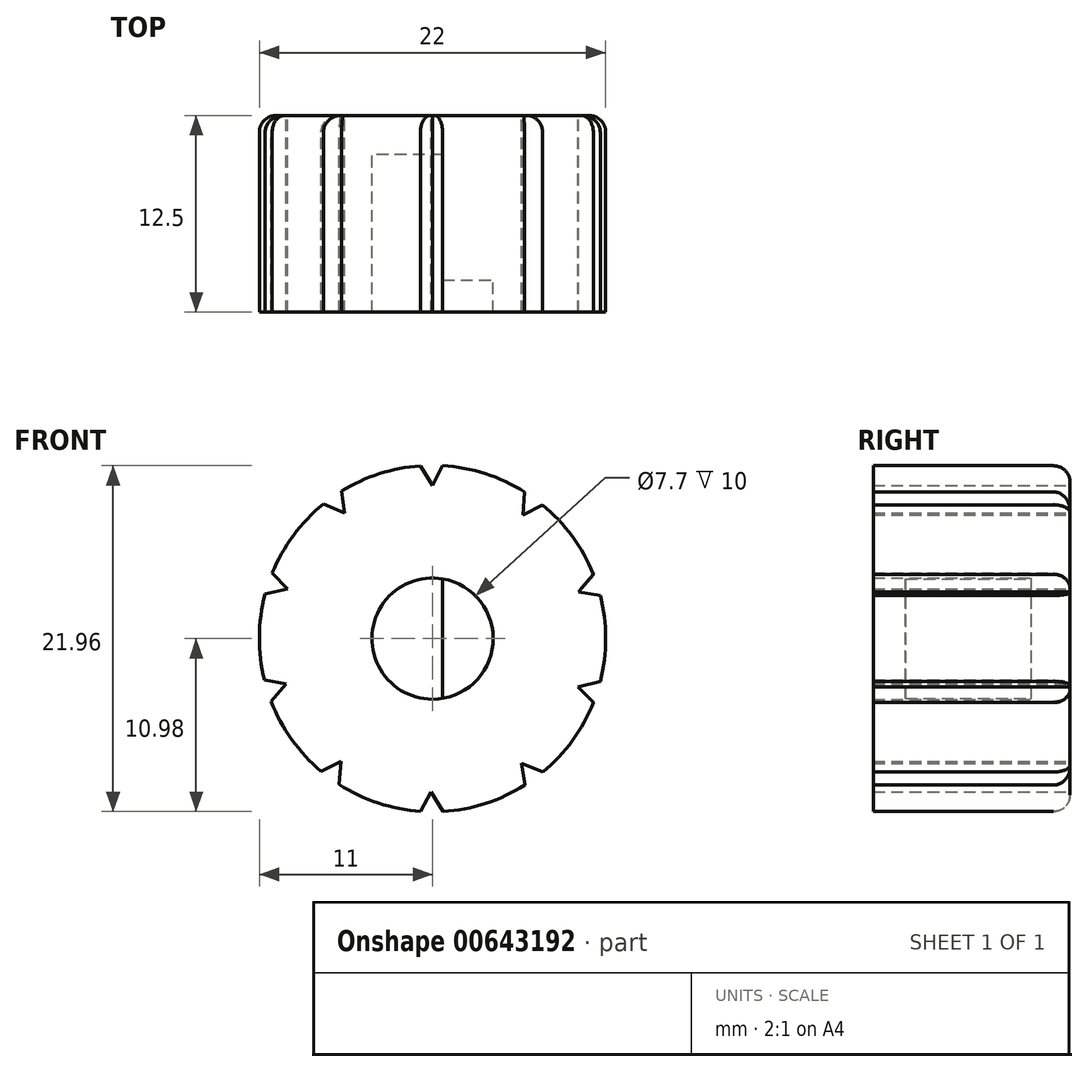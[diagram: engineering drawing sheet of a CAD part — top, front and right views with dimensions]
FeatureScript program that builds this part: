
annotation { "Feature Type Name" : "Feature", "Feature Type Description" : "" }
export const myFeature = defineFeature(function(context is Context, id is Id, definition is map)
    precondition{}
    {
        {
            var Q0;
            Q0=qCreatedBy(makeId("Front.planeOp"),FACE);
            var sketch = newSketch(context, id + "F0", { "sketchPlane" : qUnion([Q0])});
            skCircle(sketch, "E0", {"center": v(0, 0) * mm, "radius": 11 * mm});
            skCircle(sketch, "E1", {"center": v(0, 0) * mm, "radius": 3.85 * mm});
            skLineSegment(sketch, "E2", {"start": v(0.65, 3.8) * mm, "end": v(0.65, -3.8) * mm});
            skLineSegment(sketch, "E3", {"start": v(-0.77, 10.97) * mm, "end": v(0, 9.74) * mm});
            skLineSegment(sketch, "E4", {"start": v(0, 9.74) * mm, "end": v(0.64, 10.98) * mm});
            skLineSegment(sketch, "E5.1.0", {"start": v(5.74, 7.87) * mm, "end": v(6.99, 8.5) * mm});
            skLineSegment(sketch, "E5.1.1", {"start": v(5.84, 9.32) * mm, "end": v(5.74, 7.87) * mm});
            skLineSegment(sketch, "E5.2.0", {"start": v(9.27, 2.97) * mm, "end": v(10.65, 2.74) * mm});
            skLineSegment(sketch, "E5.2.1", {"start": v(10.21, 4.09) * mm, "end": v(9.27, 2.97) * mm});
            skLineSegment(sketch, "E5.3.0", {"start": v(9.24, -3.06) * mm, "end": v(10.22, -4.06) * mm});
            skLineSegment(sketch, "E5.3.1", {"start": v(10.66, -2.72) * mm, "end": v(9.24, -3.06) * mm});
            skLineSegment(sketch, "E5.4.0", {"start": v(5.66, -7.92) * mm, "end": v(5.86, -9.3) * mm});
            skLineSegment(sketch, "E5.4.1", {"start": v(7.01, -8.48) * mm, "end": v(5.66, -7.92) * mm});
            skLineSegment(sketch, "E5.5.0", {"start": v(-0.1, -9.74) * mm, "end": v(-0.75, -10.97) * mm});
            skLineSegment(sketch, "E5.5.1", {"start": v(0.67, -10.98) * mm, "end": v(-0.1, -9.74) * mm});
            skLineSegment(sketch, "E5.6.0", {"start": v(-5.81, -7.81) * mm, "end": v(-7.07, -8.43) * mm});
            skLineSegment(sketch, "E5.6.1", {"start": v(-5.93, -9.26) * mm, "end": v(-5.81, -7.81) * mm});
            skLineSegment(sketch, "E5.7.0", {"start": v(-9.3, -2.88) * mm, "end": v(-10.68, -2.64) * mm});
            skLineSegment(sketch, "E5.7.1", {"start": v(-10.25, -3.99) * mm, "end": v(-9.3, -2.88) * mm});
            skLineSegment(sketch, "E5.8.0", {"start": v(-9.21, 3.15) * mm, "end": v(-10.18, 4.16) * mm});
            skLineSegment(sketch, "E5.8.1", {"start": v(-10.63, 2.82) * mm, "end": v(-9.21, 3.15) * mm});
            skLineSegment(sketch, "E5.9.0", {"start": v(-5.58, 7.98) * mm, "end": v(-5.77, 9.36) * mm});
            skLineSegment(sketch, "E5.9.1", {"start": v(-6.93, 8.54) * mm, "end": v(-5.58, 7.98) * mm});
            skLineSegment(sketch, "E5.anchor1", {"start": v(0, 0) * mm, "end": v(0, 9.74) * mm, "construction": true});
            skLineSegment(sketch, "E5.anchor2", {"start": v(0, 0) * mm, "end": v(-5.58, 7.98) * mm, "construction": true});
            skSolve(sketch);
        }
        {
            var Q0;
            Q0=makeQuery(id+"F0.imprint","IMPRINT",FACE,{"disambiguationData":[TD([[makeQuery(id+"F0.imprint","IMPRINT",EDGE,{"derivedFrom":sQuery(id+"F0.wireOp",EDGE,"E0")}),1.0]])]});
            extrude(context, id + "F1", {"entities" : qUnion([Q0]), "depth" : 10 * mm, "offsetDistance" : 25 * mm});
        }
        {
            var Q0;
            {var subQ0=sQuery(id+"F0.wireOp",EDGE,"E2");Q0=makeQuery(id+"F0.imprint","IMPRINT",FACE,{"disambiguationData":[TD([[makeQuery(id+"F0.imprint","IMPRINT",EDGE,{"derivedFrom":subQ0}),1.0]])]});}
            extrude(context, id + "F2", {"entities" : qUnion([Q0]), "operationType" : NewBodyOperationType.ADD, "depth" : 7.95 * mm, "offsetDistance" : 25 * mm});
        }
        {
            var Q0;
            {var subQ4=sQuery(id+"F0.wireOp",EDGE,"E3");Q0=makeQuery(id+"F0.imprint","IMPRINT",FACE,{"disambiguationData":[TD([[makeQuery(id+"F0.imprint","IMPRINT",EDGE,{"derivedFrom":subQ4}),-1.0]])]});}
            var Q1;
            {var subQ0=sQuery(id+"F0.wireOp",EDGE,"E2");Q1=makeQuery(id+"F0.imprint","IMPRINT",FACE,{"disambiguationData":[TD([[makeQuery(id+"F0.imprint","IMPRINT",EDGE,{"derivedFrom":subQ0}),-1.0]])]});}
            var Q2;
            {var subQ0=sQuery(id+"F0.wireOp",EDGE,"E2");Q2=makeQuery(id+"F0.imprint","IMPRINT",FACE,{"disambiguationData":[TD([[makeQuery(id+"F0.imprint","IMPRINT",EDGE,{"derivedFrom":subQ0}),1.0]])]});}
            extrude(context, id + "F3", {"entities" : qUnion([Q0, Q1, Q2]), "operationType" : NewBodyOperationType.ADD, "oppositeDirection" : true, "depth" : 2.5 * mm, "offsetDistance" : 25 * mm});
        }
        {
            var Q0;
            {var subQ0=sQuery(id+"F0.wireOp",EDGE,"E0");Q0=makeQuery(id+"F3.opExtrude","CAP_EDGE",EDGE,{"disambiguationData":[OSD([subQ0]),TDD([makeQuery(id+"F0.imprint","IMPRINT",EDGE,{"disambiguationData":[TD([[makeQuery(id+"F0.imprint","INTERSECT",VERTEX,{"derivedFrom":[subQ0,sQuery(id+"F0.wireOp",EDGE,"E5.5.0")]}),1.0]])],"derivedFrom":subQ0})])],"isStart":false});}
            var Q1;
            {var subQ0=sQuery(id+"F0.wireOp",EDGE,"E0");Q1=makeQuery(id+"F3.opExtrude","CAP_EDGE",EDGE,{"disambiguationData":[OSD([subQ0]),TDD([makeQuery(id+"F0.imprint","IMPRINT",EDGE,{"disambiguationData":[TD([[makeQuery(id+"F0.imprint","INTERSECT",VERTEX,{"derivedFrom":[subQ0,sQuery(id+"F0.wireOp",EDGE,"E5.4.0")]}),1.0]])],"derivedFrom":subQ0})])],"isStart":false});}
            var Q2;
            {var subQ0=sQuery(id+"F0.wireOp",EDGE,"E0");Q2=makeQuery(id+"F3.opExtrude","CAP_EDGE",EDGE,{"disambiguationData":[OSD([subQ0]),TDD([makeQuery(id+"F0.imprint","IMPRINT",EDGE,{"disambiguationData":[TD([[makeQuery(id+"F0.imprint","INTERSECT",VERTEX,{"derivedFrom":[subQ0,sQuery(id+"F0.wireOp",EDGE,"E5.1.0")]}),1.0]])],"derivedFrom":subQ0})])],"isStart":false});}
            var Q3;
            {var subQ0=sQuery(id+"F0.wireOp",EDGE,"E0");Q3=makeQuery(id+"F3.opExtrude","CAP_EDGE",EDGE,{"disambiguationData":[OSD([subQ0]),TDD([makeQuery(id+"F0.imprint","IMPRINT",EDGE,{"disambiguationData":[TD([[makeQuery(id+"F0.imprint","INTERSECT",VERTEX,{"derivedFrom":[subQ0,sQuery(id+"F0.wireOp",EDGE,"E4")]}),1.0]])],"derivedFrom":subQ0})])],"isStart":false});}
            var Q4;
            {var subQ0=sQuery(id+"F0.wireOp",EDGE,"E0");Q4=makeQuery(id+"F3.opExtrude","CAP_EDGE",EDGE,{"disambiguationData":[OSD([subQ0]),TDD([makeQuery(id+"F0.imprint","IMPRINT",EDGE,{"disambiguationData":[TD([[makeQuery(id+"F0.imprint","INTERSECT",VERTEX,{"derivedFrom":[subQ0,sQuery(id+"F0.wireOp",EDGE,"E3")]}),-1.0]])],"derivedFrom":subQ0})])],"isStart":false});}
            var Q5;
            {var subQ0=sQuery(id+"F0.wireOp",EDGE,"E0");Q5=makeQuery(id+"F3.opExtrude","CAP_EDGE",EDGE,{"disambiguationData":[OSD([subQ0]),TDD([makeQuery(id+"F0.imprint","IMPRINT",EDGE,{"disambiguationData":[TD([[makeQuery(id+"F0.imprint","INTERSECT",VERTEX,{"derivedFrom":[subQ0,sQuery(id+"F0.wireOp",EDGE,"E5.8.0")]}),1.0]])],"derivedFrom":subQ0})])],"isStart":false});}
            var Q6;
            {var subQ0=sQuery(id+"F0.wireOp",EDGE,"E0");Q6=makeQuery(id+"F3.opExtrude","CAP_EDGE",EDGE,{"disambiguationData":[OSD([subQ0]),TDD([makeQuery(id+"F0.imprint","IMPRINT",EDGE,{"disambiguationData":[TD([[makeQuery(id+"F0.imprint","INTERSECT",VERTEX,{"derivedFrom":[subQ0,sQuery(id+"F0.wireOp",EDGE,"E5.7.0")]}),1.0]])],"derivedFrom":subQ0})])],"isStart":false});}
            var Q7;
            {var subQ0=sQuery(id+"F0.wireOp",EDGE,"E0");Q7=makeQuery(id+"F3.opExtrude","CAP_EDGE",EDGE,{"disambiguationData":[OSD([subQ0]),TDD([makeQuery(id+"F0.imprint","IMPRINT",EDGE,{"disambiguationData":[TD([[makeQuery(id+"F0.imprint","INTERSECT",VERTEX,{"derivedFrom":[subQ0,sQuery(id+"F0.wireOp",EDGE,"E5.6.0")]}),1.0]])],"derivedFrom":subQ0})])],"isStart":false});}
            var Q8;
            {var subQ0=sQuery(id+"F0.wireOp",EDGE,"E0");Q8=makeQuery(id+"F3.opExtrude","CAP_EDGE",EDGE,{"disambiguationData":[OSD([subQ0]),TDD([makeQuery(id+"F0.imprint","IMPRINT",EDGE,{"disambiguationData":[TD([[makeQuery(id+"F0.imprint","INTERSECT",VERTEX,{"derivedFrom":[subQ0,sQuery(id+"F0.wireOp",EDGE,"E5.3.0")]}),1.0]])],"derivedFrom":subQ0})])],"isStart":false});}
            var Q9;
            {var subQ0=sQuery(id+"F0.wireOp",EDGE,"E0");Q9=makeQuery(id+"F3.opExtrude","CAP_EDGE",EDGE,{"disambiguationData":[OSD([subQ0]),TDD([makeQuery(id+"F0.imprint","IMPRINT",EDGE,{"disambiguationData":[TD([[makeQuery(id+"F0.imprint","INTERSECT",VERTEX,{"derivedFrom":[subQ0,sQuery(id+"F0.wireOp",EDGE,"E5.2.0")]}),1.0]])],"derivedFrom":subQ0})])],"isStart":false});}
            fillet(context, id + "F4", {"entities" : qUnion([Q0, Q1, Q2, Q3, Q4, Q5, Q6, Q7, Q8, Q9]), "radius" : 1.06 * mm, "tangentPropagation" : true, "allowEdgeOverflow" : false});
        }
    });
